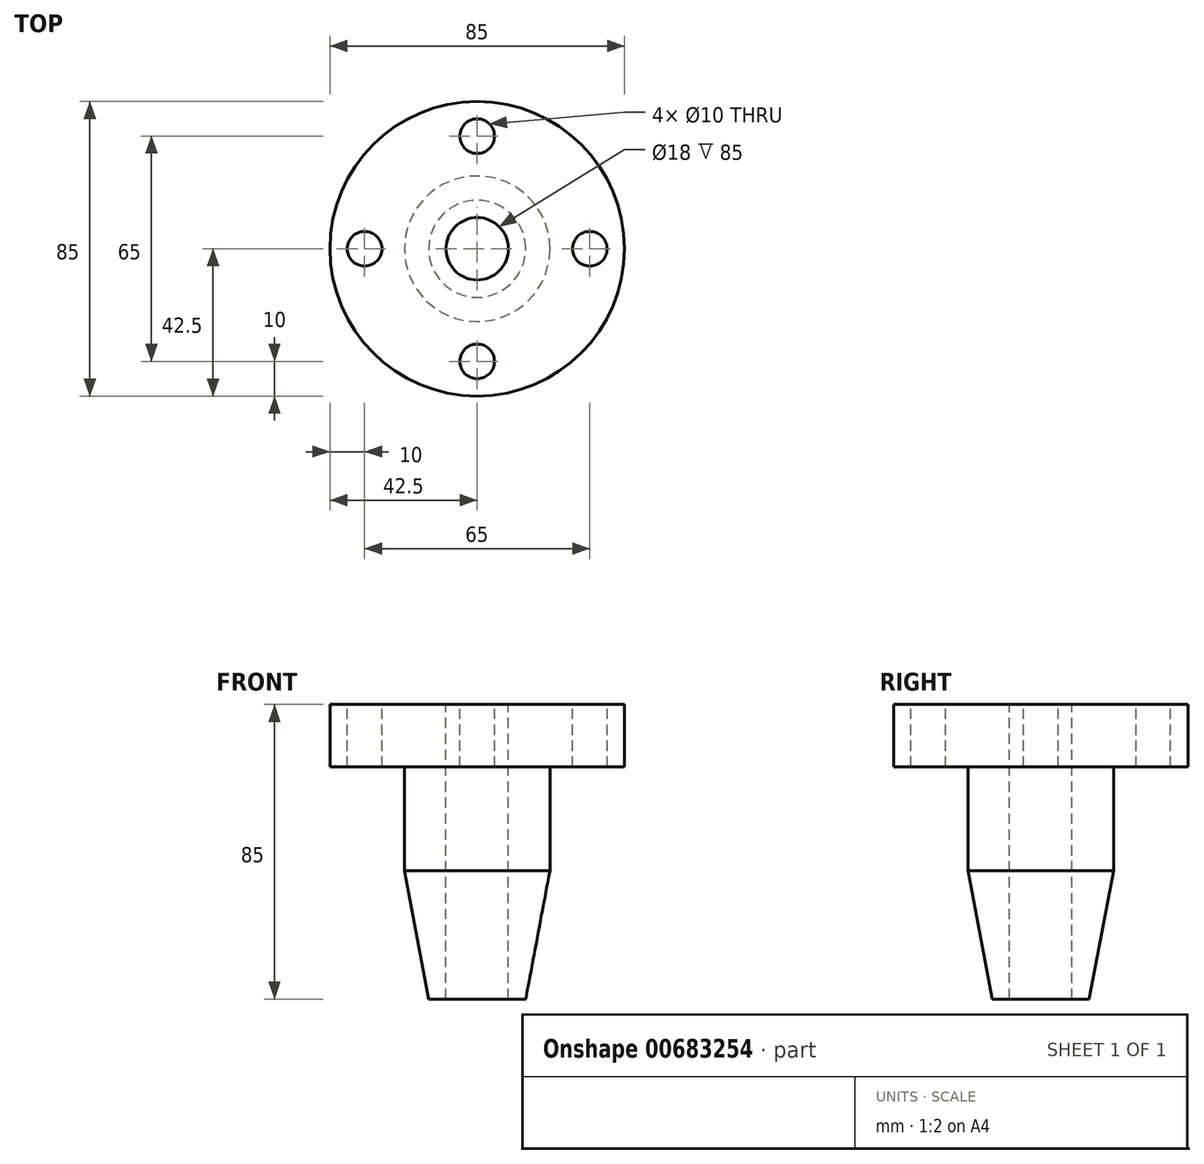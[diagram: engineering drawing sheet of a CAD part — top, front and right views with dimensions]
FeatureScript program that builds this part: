
annotation { "Feature Type Name" : "Feature", "Feature Type Description" : "" }
export const myFeature = defineFeature(function(context is Context, id is Id, definition is map)
    precondition{}
    {
        {
            var Q0;
            Q0=qCreatedBy(makeId("Front.planeOp"),FACE);
            var sketch = newSketch(context, id + "F0", { "sketchPlane" : qUnion([Q0])});
            skLineSegment(sketch, "E0", {"start": v(9, 37.37) * mm, "end": v(9, -47.63) * mm});
            skLineSegment(sketch, "E1", {"start": v(9, -47.63) * mm, "end": v(14, -47.63) * mm});
            skLineSegment(sketch, "E2", {"start": v(14, -47.63) * mm, "end": v(21, -10.63) * mm});
            skLineSegment(sketch, "E3", {"start": v(21, -10.63) * mm, "end": v(21, 19.37) * mm});
            skLineSegment(sketch, "E4", {"start": v(21, 19.37) * mm, "end": v(42.5, 19.37) * mm});
            skLineSegment(sketch, "E5", {"start": v(9, 37.37) * mm, "end": v(42.5, 37.37) * mm});
            skLineSegment(sketch, "E6", {"start": v(42.5, 19.37) * mm, "end": v(42.5, 37.37) * mm});
            skLineSegment(sketch, "E7", {"start": v(0, 50.28) * mm, "end": v(0, -63.88) * mm, "construction": true});
            skSolve(sketch);
        }
        {
            var Q0;
            Q0=makeQuery(id+"F0.imprint","IMPRINT",FACE,{"disambiguationData":[TD([[makeQuery(id+"F0.imprint","IMPRINT",EDGE,{"derivedFrom":sQuery(id+"F0.wireOp",EDGE,"E0")}),1.0]])]});
            var Q1;
            Q1=sQuery(id+"F0.wireOp",EDGE,"E7");
            revolve(context, id + "F1", {"entities" : qUnion([Q0]), "axis" : qUnion([Q1]), "revolveType" : RevolveType.FULL});
        }
        {
            var Q0;
            Q0=makeQuery(id+"F1.opRevolve","SWEPT_FACE",FACE,{"disambiguationData":[OSD([sQuery(id+"F0.wireOp",EDGE,"E5")])]});
            var sketch = newSketch(context, id + "F2", { "sketchPlane" : qUnion([Q0])});
            skSolve(sketch);
        }
        {
            var Q0;
            {var subQ0=sQuery(id+"F0.wireOp",EDGE,"E5");Q0=makeQuery(id+"F2.imprint","IMPRINT",FACE,{"disambiguationData":[TD([[makeQuery(id+"F2.imprint","IMPRINT",EDGE,{"derivedFrom":makeQuery(id+"F1.opRevolve","SWEPT_EDGE",EDGE,{"disambiguationData":[OSD([sQuery(id+"F0.wireOp",EDGE,"E0"),subQ0])]})}),-1.0]])]});}
            var sketch = newSketch(context, id + "F3", { "sketchPlane" : qUnion([Q0])});
            skCircle(sketch, "E8", {"center": v(32.5, 0) * mm, "radius": 5 * mm});
            skCircle(sketch, "E9.1.0", {"center": v(0, 32.5) * mm, "radius": 5 * mm});
            skCircle(sketch, "E9.2.0", {"center": v(-32.5, 0) * mm, "radius": 5 * mm});
            skCircle(sketch, "E9.3.0", {"center": v(0, -32.5) * mm, "radius": 5 * mm});
            skPoint(sketch, "E9.center", {"position": v(0, 0) * mm});
            skSolve(sketch);
        }
        {
            var Q0;
            Q0 = qSketchRegion(id + "F3", true);
            var Q1;
            Q1=sQuery(id+"F3.wireOp",VERTEX,"E8.center");
            extrude(context, id + "F4", {"entities" : qUnion([Q0]), "operationType" : NewBodyOperationType.REMOVE, "endBound" : BoundingType.THROUGH_ALL, "oppositeDirection" : true, "depth" : 25 * mm, "endBoundEntityVertex" : qUnion([Q1]), "offsetDistance" : 25 * mm});
        }
    });
